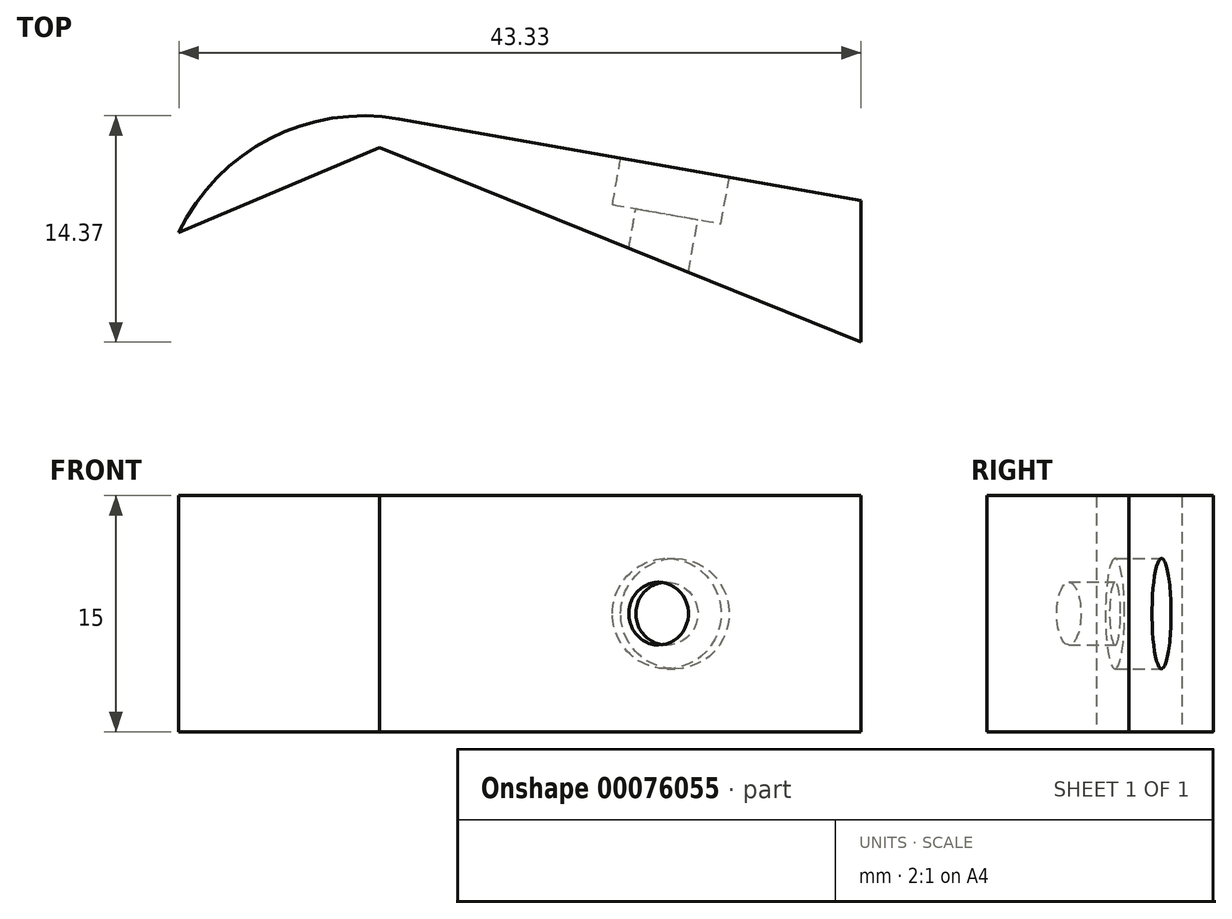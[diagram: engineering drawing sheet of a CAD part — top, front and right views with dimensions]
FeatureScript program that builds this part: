
annotation { "Feature Type Name" : "Feature", "Feature Type Description" : "" }
export const myFeature = defineFeature(function(context is Context, id is Id, definition is map)
    precondition{}
    {
        {
            var Q0;
            Q0=qCreatedBy(makeId("Top.planeOp"),FACE);
            var sketch = newSketch(context, id + "F0", { "sketchPlane" : qUnion([Q0])});
            skLineSegment(sketch, "E0", {"start": v(0, 0) * mm, "end": v(-12.73, -5.4) * mm});
            skLineSegment(sketch, "E1", {"start": v(-12.73, -5.4) * mm, "end": v(-12.73, 4.28) * mm});
            skLineSegment(sketch, "E2", {"start": v(-12.73, 4.28) * mm, "end": v(30.6, -3.36) * mm});
            skLineSegment(sketch, "E3", {"start": v(30.6, -3.36) * mm, "end": v(30.6, -12.36) * mm});
            skLineSegment(sketch, "E4", {"start": v(30.6, -12.36) * mm, "end": v(0, 0) * mm});
            skLineSegment(sketch, "E5", {"start": v(0, 0) * mm, "end": v(0, 2.03) * mm, "construction": true});
            skSolve(sketch);
        }
        {
            var Q0;
            Q0=makeQuery(id+"F0.imprint","IMPRINT",FACE,{"disambiguationData":[TD([[makeQuery(id+"F0.imprint","IMPRINT",EDGE,{"derivedFrom":sQuery(id+"F0.wireOp",EDGE,"E0")}),-1.0]])]});
            extrude(context, id + "F1", {"entities" : qUnion([Q0]), "depth" : 15 * mm});
        }
        {
            var Q0;
            Q0=makeQuery(id+"F1.opExtrude","SWEPT_EDGE",EDGE,{"disambiguationData":[OSD([sQuery(id+"F0.wireOp",EDGE,"E1"),sQuery(id+"F0.wireOp",EDGE,"E2")])]});
            fillet(context, id + "F2", {"entities" : qUnion([Q0]), "radius" : 13 * mm, "tangentPropagation" : true, "allowEdgeOverflow" : false});
        }
        {
            var Q0;
            Q0=makeQuery(id+"F1.opExtrude","SWEPT_FACE",FACE,{"disambiguationData":[OSD([sQuery(id+"F0.wireOp",EDGE,"E2")])]});
            var sketch = newSketch(context, id + "F3", { "sketchPlane" : qUnion([Q0])});
            skLineSegment(sketch, "E6", {"start": v(-0.93, 7.5) * mm, "end": v(-30.72, 7.5) * mm, "construction": true});
            skLineSegment(sketch, "E7", {"start": v(-18.72, 0) * mm, "end": v(-18.72, 15) * mm, "construction": true});
            skCircle(sketch, "E8", {"center": v(-18.72, 7.5) * mm, "radius": 2 * mm});
            skSolve(sketch);
        }
        {
            var Q0;
            Q0=makeQuery(id+"F3.imprint","IMPRINT",FACE,{"disambiguationData":[TD([[makeQuery(id+"F3.imprint","IMPRINT",EDGE,{"derivedFrom":sQuery(id+"F3.wireOp",EDGE,"E8")}),1.0]])]});
            extrude(context, id + "F4", {"entities" : qUnion([Q0]), "operationType" : NewBodyOperationType.REMOVE, "endBound" : BoundingType.THROUGH_ALL, "oppositeDirection" : true, "depth" : 25 * mm});
        }
        {
            var Q0;
            Q0=makeQuery(id+"F1.opExtrude","SWEPT_FACE",FACE,{"disambiguationData":[OSD([sQuery(id+"F0.wireOp",EDGE,"E2")])]});
            var sketch = newSketch(context, id + "F5", { "sketchPlane" : qUnion([Q0])});
            skCircle(sketch, "E9", {"center": v(-18.72, 7.5) * mm, "radius": 3.5 * mm});
            skSolve(sketch);
        }
        {
            var Q0;
            Q0=makeQuery(id+"F5.imprint","IMPRINT",FACE,{"disambiguationData":[TD([[makeQuery(id+"F5.imprint","IMPRINT",EDGE,{"derivedFrom":sQuery(id+"F5.wireOp",EDGE,"E9")}),1.0]])]});
            extrude(context, id + "F6", {"entities" : qUnion([Q0]), "operationType" : NewBodyOperationType.REMOVE, "oppositeDirection" : true, "depth" : 3 * mm});
        }
    });
